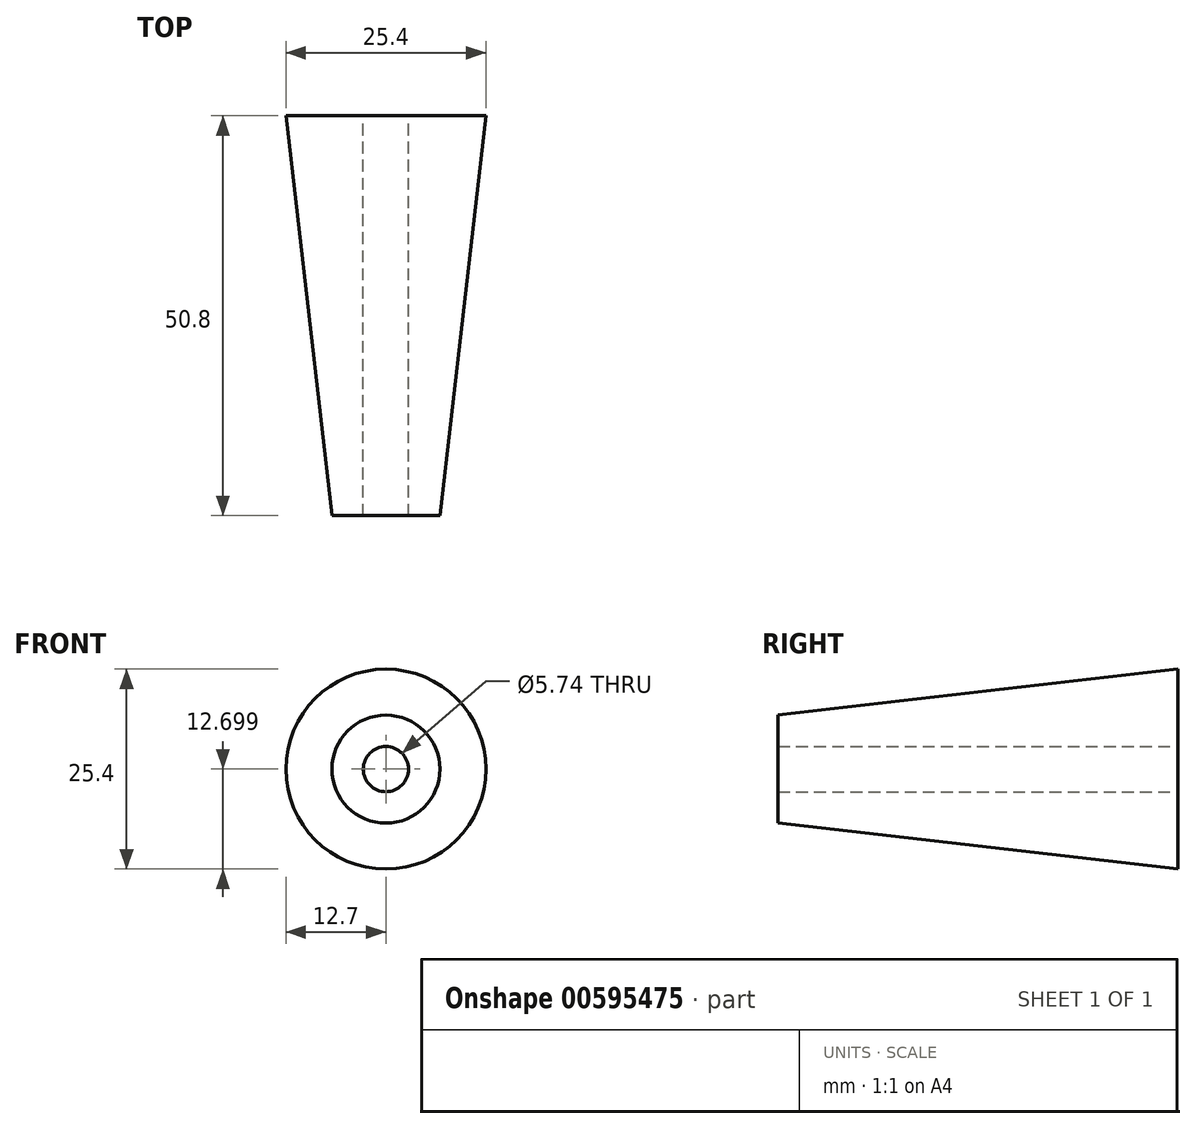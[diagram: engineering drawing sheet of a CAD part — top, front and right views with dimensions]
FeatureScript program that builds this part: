
annotation { "Feature Type Name" : "Feature", "Feature Type Description" : "" }
export const myFeature = defineFeature(function(context is Context, id is Id, definition is map)
    precondition{}
    {
        {
            var Q0;
            Q0=qCreatedBy(makeId("Front.planeOp"),FACE);
            var sketch = newSketch(context, id + "F0", { "sketchPlane" : qUnion([Q0])});
            skCircle(sketch, "E0", {"center": v(0, 0) * mm, "radius": 12.7 * mm});
            skSolve(sketch);
        }
        {
            var Q0;
            Q0=makeQuery(id+"F0.imprint","IMPRINT",FACE,{"disambiguationData":[TD([[makeQuery(id+"F0.imprint","IMPRINT",EDGE,{"derivedFrom":sQuery(id+"F0.wireOp",EDGE,"E0")}),1.0]])]});
            extrude(context, id + "F1", {"entities" : qUnion([Q0]), "depth" : 63.5 * mm, "offsetDistance" : 25.4 * mm});
        }
        {
            var Q0;
            Q0=qCreatedBy(makeId("Front.planeOp"),FACE);
            var sketch = newSketch(context, id + "F2", { "sketchPlane" : qUnion([Q0])});
            skCircle(sketch, "E1", {"center": v(0, 0) * mm, "radius": 2.87 * mm});
            skSolve(sketch);
        }
        {
            var Q0;
            Q0=sQuery(id+"F2.wireOp",VERTEX,"E1.center");
            var Q1;
            Q1=makeQuery(id+"F1.opExtrude","SWEPT_BODY",BODY,{"disambiguationData":[OSD([sQuery(id+"F0.wireOp",EDGE,"E0")])]});
            hole(context, id + "F3", {"style" : HoleStyle.SIMPLE, "endStyle" : HoleEndStyle.BLIND, "oppositeDirection" : true, "holeDiameter" : 5.74 * mm, "majorDiameter" : 6.35 * mm, "holeDepth" : 63.5 * mm, "isTappedThrough" : true, "tappedDepth" : 12.7 * mm, "tapClearance" : 3, "startFromSketch" : true, "locations" : qUnion([Q0]), "scope" : qUnion([Q1])});
        }
        {
            var Q0;
            Q0=qCreatedBy(makeId("Right.planeOp"),FACE);
            var sketch = newSketch(context, id + "F4", { "sketchPlane" : qUnion([Q0])});
            skLineSegment(sketch, "E2", {"start": v(-18.72, 40.98) * mm, "end": v(-69.52, 40.98) * mm});
            skLineSegment(sketch, "E3", {"start": v(-69.52, 40.98) * mm, "end": v(-69.52, 47.84) * mm});
            skLineSegment(sketch, "E4", {"start": v(-69.52, 47.84) * mm, "end": v(-18.72, 53.68) * mm});
            skLineSegment(sketch, "E5", {"start": v(-18.72, 53.68) * mm, "end": v(-18.72, 40.98) * mm});
            skSolve(sketch);
        }
        {
            var Q0;
            Q0=makeQuery(id+"F4.imprint","IMPRINT",FACE,{"disambiguationData":[TD([[makeQuery(id+"F4.imprint","IMPRINT",EDGE,{"derivedFrom":sQuery(id+"F4.wireOp",EDGE,"E2")}),-1.0]])]});
            var Q1;
            Q1=sQuery(id+"F4.wireOp",EDGE,"E2");
            revolve(context, id + "F5", {"entities" : qUnion([Q0]), "axis" : qUnion([Q1]), "revolveType" : RevolveType.FULL});
        }
        {
            var Q0;
            Q0=makeQuery(id+"F5.opRevolve","SWEPT_FACE",FACE,{"disambiguationData":[OSD([sQuery(id+"F4.wireOp",EDGE,"E5")])]});
            var sketch = newSketch(context, id + "F6", { "sketchPlane" : qUnion([Q0])});
            skPoint(sketch, "E6", {"position": v(0, 40.98) * mm});
            skSolve(sketch);
        }
        {
            var Q0;
            Q0=sQuery(id+"F6.wireOp",VERTEX,"E6");
            var Q1;
            Q1=makeQuery(id+"F5.opRevolve","SWEPT_BODY",BODY,{"disambiguationData":[OSD([sQuery(id+"F4.wireOp",EDGE,"E2"),sQuery(id+"F4.wireOp",EDGE,"E3"),sQuery(id+"F4.wireOp",EDGE,"E4"),sQuery(id+"F4.wireOp",EDGE,"E5")])]});
            hole(context, id + "F7", {"style" : HoleStyle.SIMPLE, "endStyle" : HoleEndStyle.BLIND, "holeDiameter" : 5.74 * mm, "majorDiameter" : 6.35 * mm, "holeDepth" : 50.8 * mm, "isTappedThrough" : true, "tappedDepth" : 12.7 * mm, "tapClearance" : 3, "startFromSketch" : true, "locations" : qUnion([Q0]), "scope" : qUnion([Q1])});
        }
        {
            var Q0;
            Q0=makeQuery(id+"F1.opExtrude","SWEPT_BODY",BODY,{"disambiguationData":[OSD([sQuery(id+"F0.wireOp",EDGE,"E0")])]});
            deleteBodies(context, id + "F8", {"entities" : qUnion([Q0])});
        }
    });
